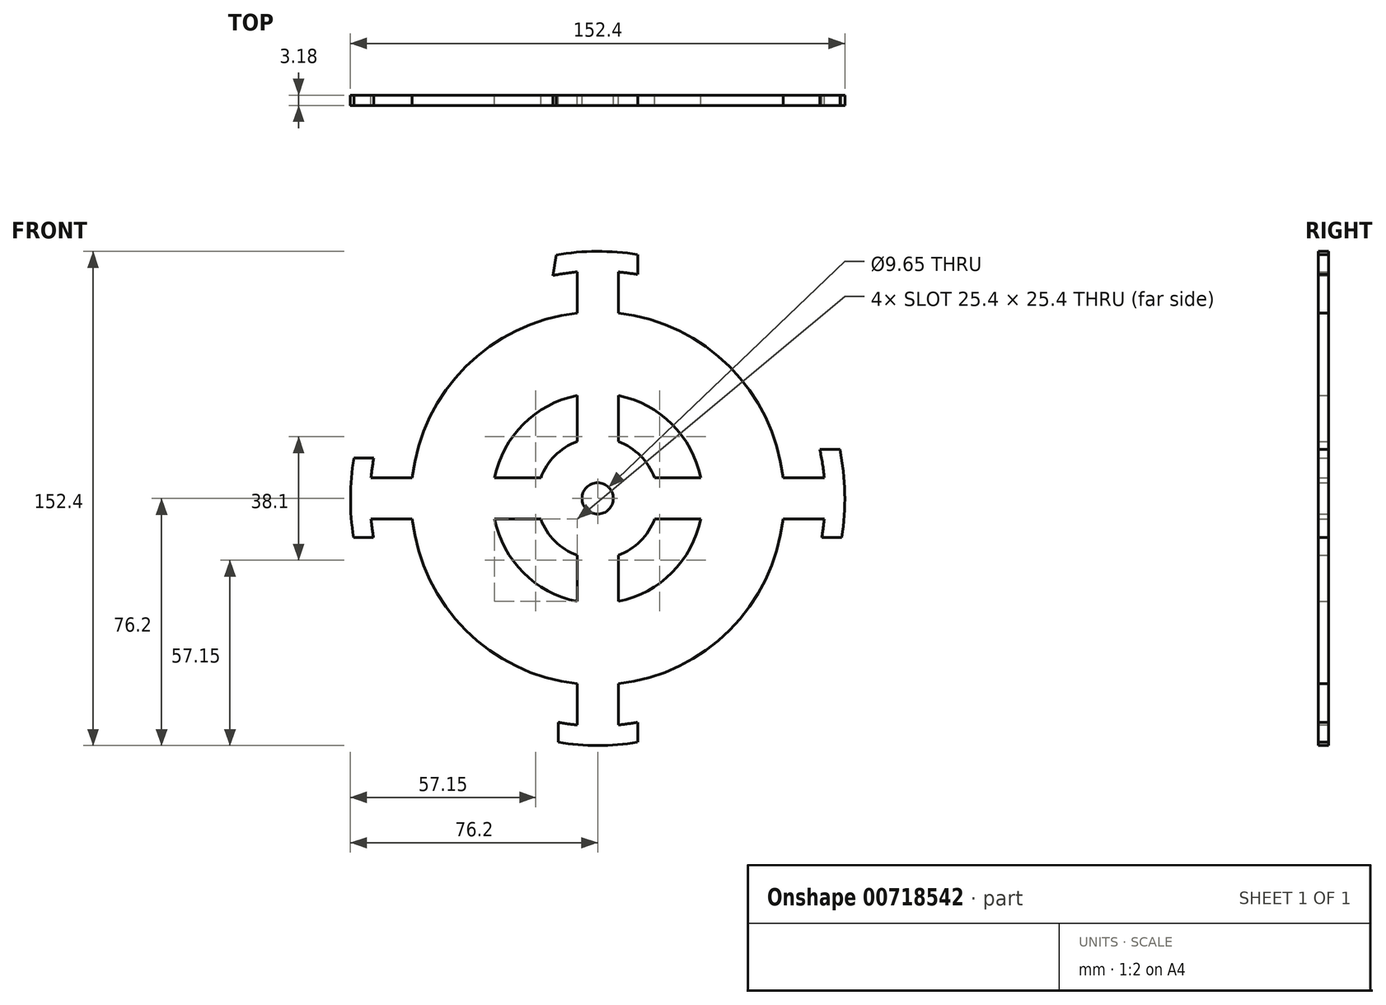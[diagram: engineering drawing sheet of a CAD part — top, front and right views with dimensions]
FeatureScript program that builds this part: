
annotation { "Feature Type Name" : "Feature", "Feature Type Description" : "" }
export const myFeature = defineFeature(function(context is Context, id is Id, definition is map)
    precondition{}
    {
        {
            var Q0;
            Q0=qCreatedBy(makeId("Front.planeOp"),FACE);
            var sketch = newSketch(context, id + "F0", { "sketchPlane" : qUnion([Q0])});
            skCircle(sketch, "E0", {"center": v(0, 0) * mm, "radius": 76.2 * mm});
            skCircle(sketch, "E1", {"center": v(0, 0) * mm, "radius": 63.5 * mm, "construction": true});
            skCircle(sketch, "E2", {"center": v(0, 0) * mm, "radius": 4.83 * mm});
            skLineSegment(sketch, "E3", {"start": v(-76.2, 0) * mm, "end": v(76.2, 0) * mm, "construction": true});
            skLineSegment(sketch, "E4", {"start": v(0, -76.2) * mm, "end": v(0, 76.2) * mm, "construction": true});
            skPoint(sketch, "E5", {"position": v(17.53, 0) * mm});
            skPoint(sketch, "E6", {"position": v(-17.53, 0) * mm});
            skPoint(sketch, "E7", {"position": v(0, 17.53) * mm});
            skPoint(sketch, "E8", {"position": v(0, -17.53) * mm});
            skPoint(sketch, "E9", {"position": v(-69.85, 0) * mm});
            skPoint(sketch, "E10", {"position": v(-57.15, 0) * mm});
            skPoint(sketch, "E11", {"position": v(0, 69.85) * mm});
            skPoint(sketch, "E12", {"position": v(0, 57.15) * mm});
            skPoint(sketch, "E13", {"position": v(0, -57.15) * mm});
            skPoint(sketch, "E14", {"position": v(0, -69.85) * mm});
            skPoint(sketch, "E15", {"position": v(57.15, 0) * mm});
            skPoint(sketch, "E16", {"position": v(69.85, 0) * mm});
            skPoint(sketch, "E17", {"position": v(0, 31.75) * mm});
            skPoint(sketch, "E18", {"position": v(-31.75, 0) * mm});
            skPoint(sketch, "E19", {"position": v(0, -31.75) * mm});
            skPoint(sketch, "E20", {"position": v(31.75, 0) * mm});
            skLineSegment(sketch, "E21", {"start": v(-69.85, 0) * mm, "end": v(-69.85, 6.35) * mm, "construction": true});
            skLineSegment(sketch, "E22", {"start": v(0, -69.85) * mm, "end": v(6.35, -69.85) * mm, "construction": true});
            skLineSegment(sketch, "E23", {"start": v(0, -69.85) * mm, "end": v(-6.35, -69.85) * mm, "construction": true});
            skLineSegment(sketch, "E24", {"start": v(69.85, 0) * mm, "end": v(69.85, 6.35) * mm, "construction": true});
            skLineSegment(sketch, "E25", {"start": v(69.85, 0) * mm, "end": v(69.85, -6.35) * mm, "construction": true});
            skLineSegment(sketch, "E26", {"start": v(0, 31.75) * mm, "end": v(-6.35, 31.75) * mm, "construction": true});
            skLineSegment(sketch, "E27", {"start": v(0, 31.75) * mm, "end": v(6.35, 31.75) * mm, "construction": true});
            skLineSegment(sketch, "E28", {"start": v(0, 57.15) * mm, "end": v(6.35, 57.15) * mm, "construction": true});
            skLineSegment(sketch, "E29", {"start": v(0, 57.15) * mm, "end": v(-6.35, 57.15) * mm, "construction": true});
            skLineSegment(sketch, "E30", {"start": v(0, 69.85) * mm, "end": v(6.35, 69.85) * mm, "construction": true});
            skLineSegment(sketch, "E31", {"start": v(0, 69.85) * mm, "end": v(-6.35, 69.85) * mm, "construction": true});
            skLineSegment(sketch, "E32", {"start": v(-69.85, 0) * mm, "end": v(-69.85, -6.35) * mm, "construction": true});
            skLineSegment(sketch, "E33", {"start": v(-57.15, 0) * mm, "end": v(-57.15, 6.35) * mm, "construction": true});
            skLineSegment(sketch, "E34", {"start": v(-57.15, 0) * mm, "end": v(-57.15, -6.35) * mm, "construction": true});
            skLineSegment(sketch, "E35", {"start": v(-31.75, 0) * mm, "end": v(-31.75, 6.35) * mm, "construction": true});
            skLineSegment(sketch, "E36", {"start": v(-31.75, 0) * mm, "end": v(-31.75, -6.35) * mm, "construction": true});
            skLineSegment(sketch, "E37", {"start": v(0, 17.53) * mm, "end": v(-6.35, 17.53) * mm, "construction": true});
            skLineSegment(sketch, "E38", {"start": v(-17.53, 0) * mm, "end": v(-17.53, 6.35) * mm, "construction": true});
            skLineSegment(sketch, "E39", {"start": v(-17.53, 0) * mm, "end": v(-17.53, -6.35) * mm, "construction": true});
            skLineSegment(sketch, "E40", {"start": v(17.53, 0) * mm, "end": v(17.53, -6.35) * mm, "construction": true});
            skLineSegment(sketch, "E41", {"start": v(17.53, 0) * mm, "end": v(17.53, 6.35) * mm, "construction": true});
            skLineSegment(sketch, "E42", {"start": v(31.75, 0) * mm, "end": v(31.75, 6.35) * mm, "construction": true});
            skLineSegment(sketch, "E43", {"start": v(31.75, 0) * mm, "end": v(31.75, -6.35) * mm, "construction": true});
            skLineSegment(sketch, "E44", {"start": v(57.15, 0) * mm, "end": v(57.15, 6.35) * mm, "construction": true});
            skLineSegment(sketch, "E45", {"start": v(57.15, 0) * mm, "end": v(57.15, -6.35) * mm, "construction": true});
            skLineSegment(sketch, "E46", {"start": v(0, -31.75) * mm, "end": v(6.35, -31.75) * mm, "construction": true});
            skLineSegment(sketch, "E47", {"start": v(0, -31.75) * mm, "end": v(-6.35, -31.75) * mm, "construction": true});
            skLineSegment(sketch, "E48", {"start": v(0, -57.15) * mm, "end": v(6.35, -57.15) * mm, "construction": true});
            skLineSegment(sketch, "E49", {"start": v(0, -57.15) * mm, "end": v(-6.35, -57.15) * mm, "construction": true});
            skLineSegment(sketch, "E50", {"start": v(0, -17.53) * mm, "end": v(6.35, -17.53) * mm, "construction": true});
            skLineSegment(sketch, "E51", {"start": v(0, -17.53) * mm, "end": v(-6.35, -17.53) * mm, "construction": true});
            skLineSegment(sketch, "E52", {"start": v(0, 17.53) * mm, "end": v(6.35, 17.53) * mm, "construction": true});
            skArc(sketch, "E53", {"start": v(-17.53, -6.35) * mm, "mid": v(-13.18, -13.18) * mm, "end": v(-6.35, -17.53) * mm});
            skArc(sketch, "E54", {"start": v(6.35, -17.53) * mm, "mid": v(13.18, -13.18) * mm, "end": v(17.53, -6.35) * mm});
            skArc(sketch, "E55", {"start": v(17.53, 6.35) * mm, "mid": v(13.18, 13.18) * mm, "end": v(6.35, 17.53) * mm});
            skArc(sketch, "E56", {"start": v(-6.35, 17.53) * mm, "mid": v(-13.18, 13.18) * mm, "end": v(-17.53, 6.35) * mm});
            skArc(sketch, "E57", {"start": v(-6.35, 31.75) * mm, "mid": v(-22.9, 22.9) * mm, "end": v(-31.75, 6.35) * mm});
            skArc(sketch, "E58", {"start": v(6.35, 31.75) * mm, "mid": v(22.9, 22.9) * mm, "end": v(31.75, 6.35) * mm});
            skArc(sketch, "E59", {"start": v(-31.75, -6.35) * mm, "mid": v(-22.9, -22.9) * mm, "end": v(-6.35, -31.75) * mm});
            skArc(sketch, "E60", {"start": v(6.35, -31.75) * mm, "mid": v(22.9, -22.9) * mm, "end": v(31.75, -6.35) * mm});
            skArc(sketch, "E61", {"start": v(6.35, 57.15) * mm, "mid": v(40.66, 40.66) * mm, "end": v(57.15, 6.35) * mm});
            skArc(sketch, "E62", {"start": v(57.15, -6.35) * mm, "mid": v(40.66, -40.66) * mm, "end": v(6.35, -57.15) * mm});
            skArc(sketch, "E63", {"start": v(-6.35, -57.15) * mm, "mid": v(-40.66, -40.66) * mm, "end": v(-57.15, -6.35) * mm});
            skArc(sketch, "E64", {"start": v(-57.15, 6.35) * mm, "mid": v(-40.66, 40.66) * mm, "end": v(-6.35, 57.15) * mm});
            skLineSegment(sketch, "E65", {"start": v(-6.35, 17.53) * mm, "end": v(-6.35, 31.75) * mm});
            skLineSegment(sketch, "E66", {"start": v(6.35, 17.53) * mm, "end": v(6.35, 31.75) * mm});
            skLineSegment(sketch, "E67", {"start": v(6.35, 57.15) * mm, "end": v(6.35, 69.85) * mm});
            skLineSegment(sketch, "E68", {"start": v(-6.35, 57.15) * mm, "end": v(-6.35, 69.85) * mm});
            skLineSegment(sketch, "E69", {"start": v(6.35, -17.53) * mm, "end": v(6.35, -31.75) * mm});
            skLineSegment(sketch, "E70", {"start": v(-6.35, -17.53) * mm, "end": v(-6.35, -31.75) * mm});
            skLineSegment(sketch, "E71", {"start": v(-6.35, -57.15) * mm, "end": v(-6.35, -69.85) * mm});
            skLineSegment(sketch, "E72", {"start": v(6.35, -57.15) * mm, "end": v(6.35, -69.85) * mm});
            skLineSegment(sketch, "E73", {"start": v(31.75, -6.35) * mm, "end": v(17.53, -6.35) * mm});
            skLineSegment(sketch, "E74", {"start": v(17.53, 6.35) * mm, "end": v(31.75, 6.35) * mm});
            skLineSegment(sketch, "E75", {"start": v(57.15, 6.35) * mm, "end": v(69.85, 6.35) * mm});
            skLineSegment(sketch, "E76", {"start": v(57.15, -6.35) * mm, "end": v(69.85, -6.35) * mm});
            skLineSegment(sketch, "E77", {"start": v(-17.53, -6.35) * mm, "end": v(-31.75, -6.35) * mm});
            skLineSegment(sketch, "E78", {"start": v(-31.75, 6.35) * mm, "end": v(-17.53, 6.35) * mm});
            skLineSegment(sketch, "E79", {"start": v(-57.15, -6.35) * mm, "end": v(-69.85, -6.35) * mm});
            skLineSegment(sketch, "E80", {"start": v(-69.85, 6.35) * mm, "end": v(-57.15, 6.35) * mm});
            skArc(sketch, "E81", {"start": v(-6.35, 69.85) * mm, "mid": v(-49.6, 49.6) * mm, "end": v(-69.85, 6.35) * mm});
            skArc(sketch, "E82", {"start": v(-69.85, -6.35) * mm, "mid": v(-49.6, -49.6) * mm, "end": v(-6.35, -69.85) * mm});
            skArc(sketch, "E83", {"start": v(6.35, -69.85) * mm, "mid": v(49.6, -49.6) * mm, "end": v(69.85, -6.35) * mm});
            skArc(sketch, "E84", {"start": v(6.35, 69.85) * mm, "mid": v(49.6, 49.6) * mm, "end": v(69.85, 6.35) * mm});
            skSolve(sketch);
        }
        {
            var Q0;
            Q0 = qSketchRegion(id + "F0", true);
            extrude(context, id + "F1", {"entities" : qUnion([Q0]), "depth" : 3.17 * mm, "offsetDistance" : 25.4 * mm});
        }
        {
            var Q0;
            Q0=makeQuery(id+"F1.opExtrude","CAP_FACE",FACE,{"disambiguationData":[OSD([sQuery(id+"F0.wireOp",EDGE,"E0"),sQuery(id+"F0.wireOp",EDGE,"E2"),sQuery(id+"F0.wireOp",EDGE,"E53"),sQuery(id+"F0.wireOp",EDGE,"E54"),sQuery(id+"F0.wireOp",EDGE,"E55"),sQuery(id+"F0.wireOp",EDGE,"E56"),sQuery(id+"F0.wireOp",EDGE,"E57"),sQuery(id+"F0.wireOp",EDGE,"E58"),sQuery(id+"F0.wireOp",EDGE,"E59"),sQuery(id+"F0.wireOp",EDGE,"E60"),sQuery(id+"F0.wireOp",EDGE,"E61"),sQuery(id+"F0.wireOp",EDGE,"E62"),sQuery(id+"F0.wireOp",EDGE,"E63"),sQuery(id+"F0.wireOp",EDGE,"E64"),sQuery(id+"F0.wireOp",EDGE,"E65"),sQuery(id+"F0.wireOp",EDGE,"E66"),sQuery(id+"F0.wireOp",EDGE,"E67"),sQuery(id+"F0.wireOp",EDGE,"E68"),sQuery(id+"F0.wireOp",EDGE,"E69"),sQuery(id+"F0.wireOp",EDGE,"E70"),sQuery(id+"F0.wireOp",EDGE,"E71"),sQuery(id+"F0.wireOp",EDGE,"E72"),sQuery(id+"F0.wireOp",EDGE,"E73"),sQuery(id+"F0.wireOp",EDGE,"E74"),sQuery(id+"F0.wireOp",EDGE,"E75"),sQuery(id+"F0.wireOp",EDGE,"E76"),sQuery(id+"F0.wireOp",EDGE,"E77"),sQuery(id+"F0.wireOp",EDGE,"E78"),sQuery(id+"F0.wireOp",EDGE,"E79"),sQuery(id+"F0.wireOp",EDGE,"E80"),sQuery(id+"F0.wireOp",EDGE,"E81"),sQuery(id+"F0.wireOp",EDGE,"E82"),sQuery(id+"F0.wireOp",EDGE,"E83"),sQuery(id+"F0.wireOp",EDGE,"E84")])],"isStart":false});
            var sketch = newSketch(context, id + "F2", { "sketchPlane" : qUnion([Q0])});
            skLineSegment(sketch, "E85", {"start": v(-65.22, 12.46) * mm, "end": v(-81.83, 12.46) * mm});
            skLineSegment(sketch, "E86", {"start": v(-81.83, 12.46) * mm, "end": v(-54.43, 65.5) * mm});
            skLineSegment(sketch, "E87", {"start": v(-54.43, 65.5) * mm, "end": v(-12.17, 78.92) * mm});
            skLineSegment(sketch, "E88", {"start": v(-12.17, 78.92) * mm, "end": v(-14.5, 64.34) * mm});
            skLineSegment(sketch, "E89", {"start": v(-14.5, 64.34) * mm, "end": v(-44.52, 45.1) * mm});
            skLineSegment(sketch, "E90", {"start": v(-44.52, 45.1) * mm, "end": v(-65.22, 12.46) * mm});
            skLineSegment(sketch, "E91", {"start": v(12.31, 63.47) * mm, "end": v(44.67, 47.15) * mm});
            skLineSegment(sketch, "E92", {"start": v(44.67, 47.15) * mm, "end": v(63.32, 15.08) * mm});
            skLineSegment(sketch, "E93", {"start": v(63.32, 15.08) * mm, "end": v(85.18, 15.08) * mm});
            skLineSegment(sketch, "E94", {"start": v(85.18, 15.08) * mm, "end": v(62.16, 64.63) * mm});
            skLineSegment(sketch, "E95", {"start": v(62.16, 64.63) * mm, "end": v(12.31, 79.5) * mm});
            skLineSegment(sketch, "E96", {"start": v(12.31, 79.5) * mm, "end": v(12.31, 63.47) * mm});
            skLineSegment(sketch, "E97", {"start": v(63.61, -12.02) * mm, "end": v(91.6, -12.02) * mm});
            skLineSegment(sketch, "E98", {"start": v(91.6, -12.02) * mm, "end": v(57.15, -66.82) * mm});
            skLineSegment(sketch, "E99", {"start": v(57.15, -66.82) * mm, "end": v(12.31, -79.35) * mm});
            skLineSegment(sketch, "E100", {"start": v(12.31, -79.35) * mm, "end": v(12.31, -61) * mm});
            skLineSegment(sketch, "E101", {"start": v(12.31, -61) * mm, "end": v(48.46, -43.8) * mm});
            skLineSegment(sketch, "E102", {"start": v(48.46, -43.8) * mm, "end": v(63.61, -12.02) * mm});
            skLineSegment(sketch, "E103", {"start": v(-12.17, -63.5) * mm, "end": v(-12.17, -78.77) * mm});
            skPoint(sketch, "E103.startSnap0", {"position": v(-6.35, -63.5) * mm});
            skLineSegment(sketch, "E104", {"start": v(-12.17, -78.77) * mm, "end": v(-63.18, -61) * mm});
            skLineSegment(sketch, "E105", {"start": v(-63.18, -61) * mm, "end": v(-76.88, -30.97) * mm});
            skLineSegment(sketch, "E106", {"start": v(-76.88, -30.97) * mm, "end": v(-81.25, -12.02) * mm});
            skLineSegment(sketch, "E107", {"start": v(-81.25, -12.02) * mm, "end": v(-63.18, -12.02) * mm});
            skLineSegment(sketch, "E108", {"start": v(-63.18, -12.02) * mm, "end": v(-48.31, -43.8) * mm});
            skLineSegment(sketch, "E109", {"start": v(-48.31, -43.8) * mm, "end": v(-12.17, -63.5) * mm});
            skSolve(sketch);
        }
        {
            var Q0;
            Q0 = qSketchRegion(id + "F2", true);
            extrude(context, id + "F3", {"entities" : qUnion([Q0]), "operationType" : NewBodyOperationType.REMOVE, "oppositeDirection" : true, "depth" : 25.4 * mm, "offsetDistance" : 25.4 * mm});
        }
    });
